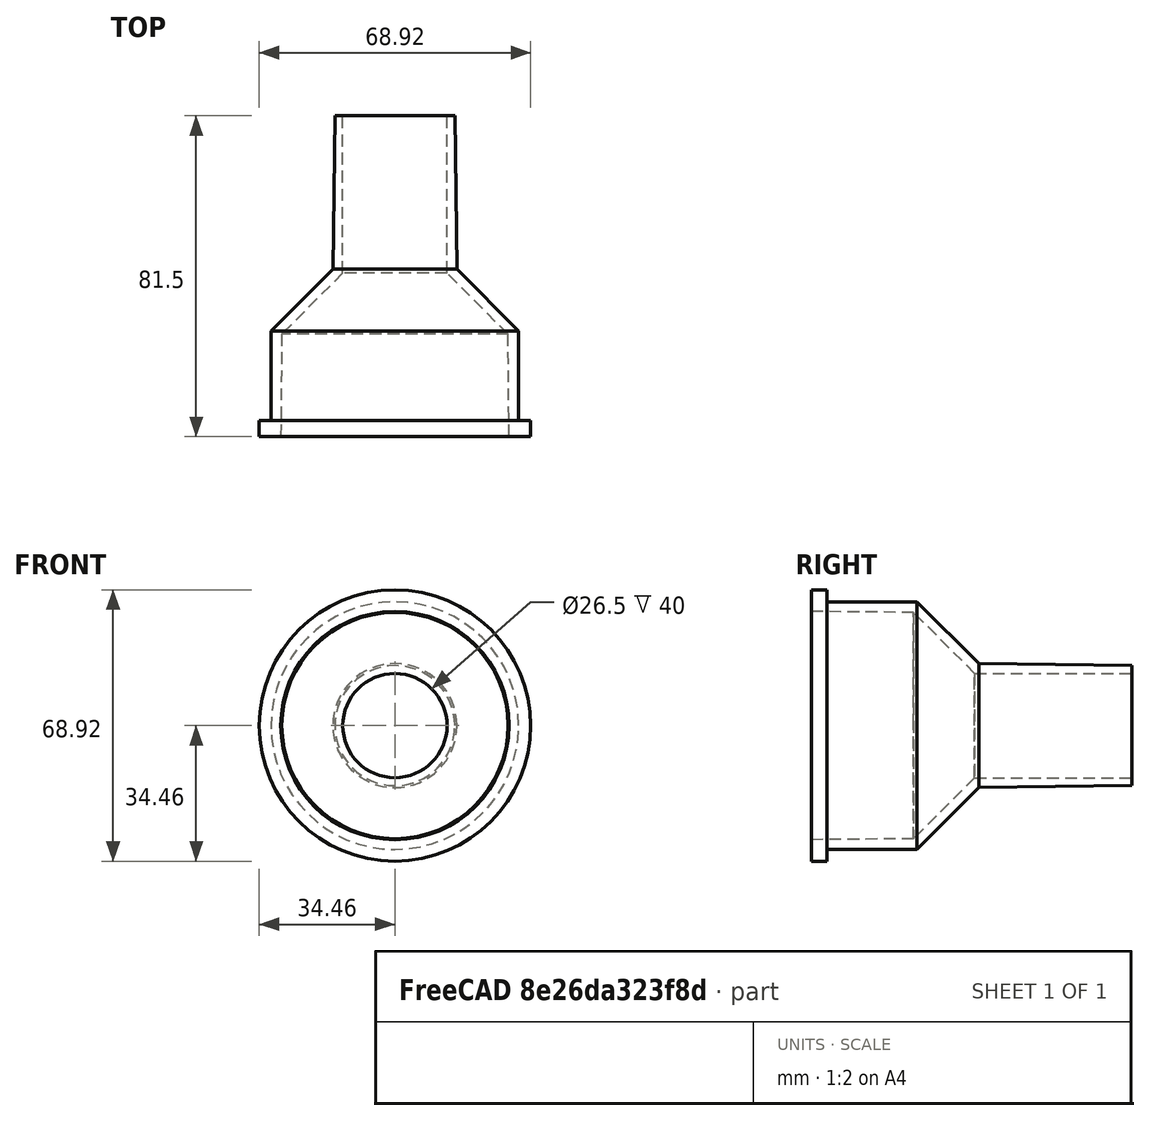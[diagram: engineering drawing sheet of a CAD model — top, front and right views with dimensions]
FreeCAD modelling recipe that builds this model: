
FCSTD DOCUMENT  (FreeCAD 0.16R)
Label: CarVacAdapter
License: All rights reserved
LicenseURL: http://en.wikipedia.org/wiki/All_rights_reserved
objects: Sketcher::SketchObject×1, PartDesign::Revolution×1, Mesh::Feature×1
note: 3 computed .brp shape members not serialized (recipe doc carries the construction recipe); baked Part::Feature solids carry a one-line shape summary decoded from their .brp

FEATURE [Sketcher::SketchObject] Sketch
  sketch-geometry (10):
    g0: LineSegment StartX=29 StartY=0 StartZ=0 EndX=28.75 EndY=26 EndZ=0
    g1: LineSegment StartX=28.75 StartY=26 StartZ=0 EndX=13.25 EndY=41.5 EndZ=0
    g2: LineSegment StartX=13.25 StartY=41.5 StartZ=0 EndX=13.25 EndY=81.5 EndZ=0
    g3: LineSegment StartX=13.25 StartY=81.5 StartZ=0 EndX=15.25 EndY=81.5 EndZ=0
    g4: LineSegment StartX=15.25 StartY=81.5 StartZ=0 EndX=15.75 EndY=42.5355 EndZ=0
    g5: LineSegment StartX=15.75 StartY=42.5355 StartZ=0 EndX=31.4617 EndY=26.8239 EndZ=0
    g6: LineSegment StartX=31.4617 StartY=26.8239 StartZ=0 EndX=31.4617 EndY=4 EndZ=0
    g7: LineSegment StartX=31.4617 StartY=4 StartZ=0 EndX=34.4617 EndY=4 EndZ=0
    g8: LineSegment StartX=34.4617 StartY=4 StartZ=0 EndX=34.4617 EndY=0 EndZ=0
    g9: LineSegment StartX=34.4617 StartY=0 StartZ=0 EndX=29 EndY=0 EndZ=0
  constraints (31):
    c: PointOnObject(g0,g-1)
    c: Coincident(g0,g1)
    c: Coincident(g1,g2)
    c: Vertical(g2)
    c: Coincident(g2,g3)
    c: Horizontal(g3)
    c: Coincident(g3,g4)
    c: Coincident(g4,g5)
    c: Coincident(g5,g6)
    c: Vertical(g6)
    c: Coincident(g6,g7)
    c: Coincident(g7,g8)
    c: PointOnObject(g8,g-1)
    c: Vertical(g8)
    c: Coincident(g8,g9)
    c: Horizontal(g9)
    c: Coincident(g9,g0)
    c: DistanceX(g3) = 15.25
    c: DistanceX(g4) = 15.75
    c: Distance(g3) = 2
    c: DistanceX(g0) = 28.75
    c: DistanceX(g0) = 29
    c: DistanceY(g0) = 26
    c: Horizontal(g7)
    c: Distance(g6,g0) = 2.5
    c: Distance(g7) = 3
    c: Parallel(g1,g5)
    c: Angle(g1) = 2.35619
    c: Distance(g2) = 40
    c: DistanceY(g6) = 4
    c: Distance(g4,g1) = 2.5
FEATURE [PartDesign::Revolution] Revolution
  Angle = 360
  Axis = (0,1,0)
  Base = (0,0,0)
  ReferenceAxis = -> Sketch [V_Axis]
  Reversed = true
  Sketch = -> Sketch
FEATURE [Mesh::Feature] Mesh  label="Revolution (Meshed)"
